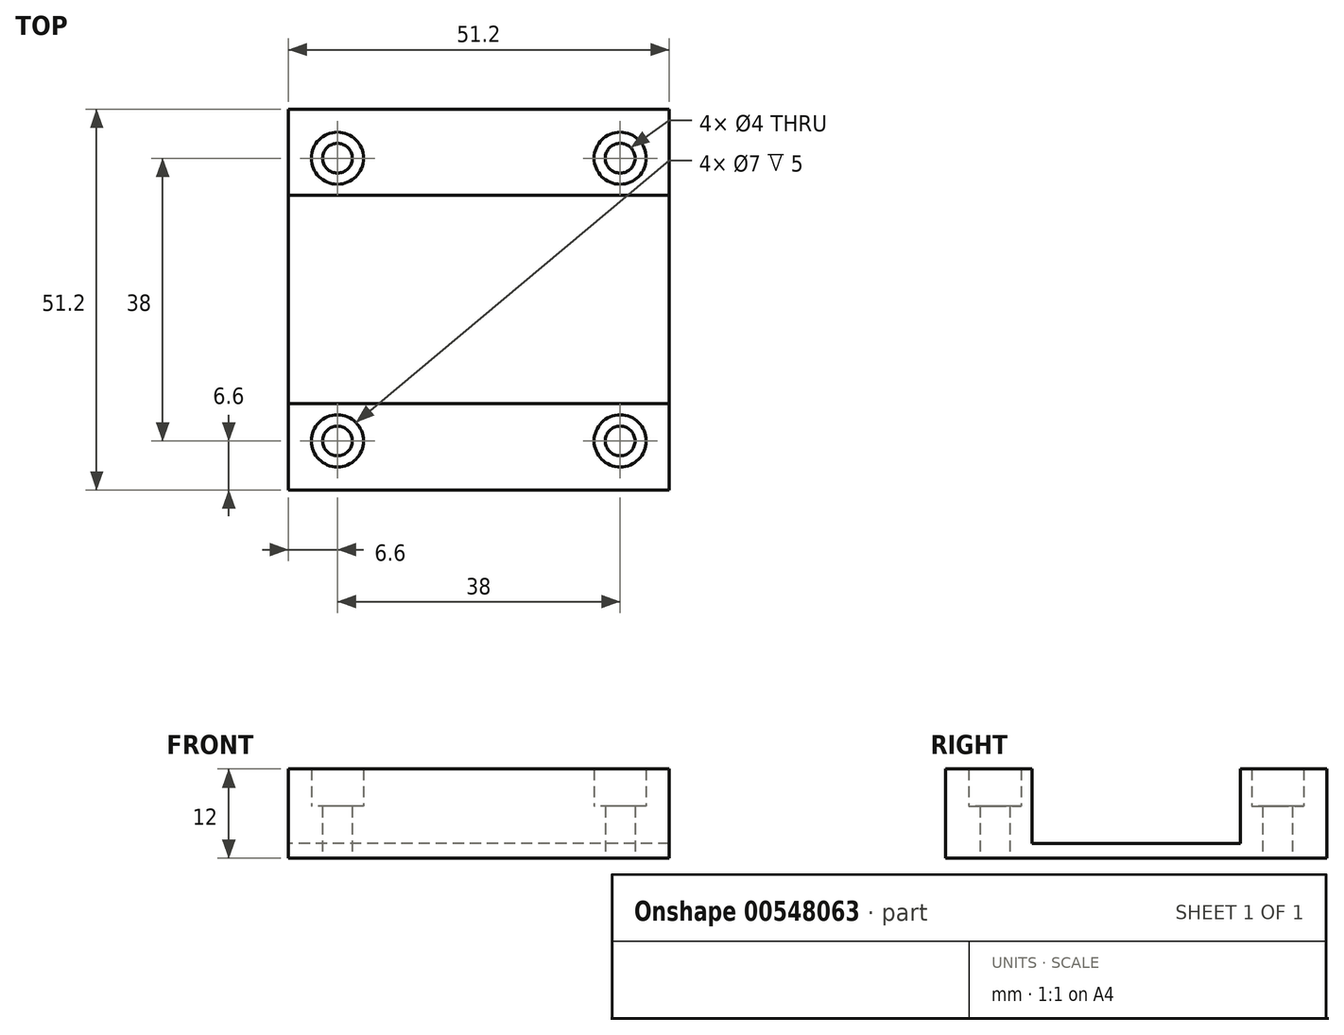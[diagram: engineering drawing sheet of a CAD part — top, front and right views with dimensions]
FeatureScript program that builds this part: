
annotation { "Feature Type Name" : "Feature", "Feature Type Description" : "" }
export const myFeature = defineFeature(function(context is Context, id is Id, definition is map)
    precondition{}
    {
        {
            var Q0;
            Q0=qCreatedBy(makeId("Top.planeOp"),FACE);
            var sketch = newSketch(context, id + "F0", { "sketchPlane" : qUnion([Q0])});
            skLineSegment(sketch, "E0.bottom", {"start": v(-25.6, 25.6) * mm, "end": v(25.6, 25.6) * mm});
            skLineSegment(sketch, "E0.top", {"start": v(-25.6, -25.6) * mm, "end": v(25.6, -25.6) * mm});
            skLineSegment(sketch, "E0.left", {"start": v(-25.6, 25.6) * mm, "end": v(-25.6, -25.6) * mm});
            skLineSegment(sketch, "E0.right", {"start": v(25.6, 25.6) * mm, "end": v(25.6, -25.6) * mm});
            skLineSegment(sketch, "E1", {"start": v(-25.6, 25.6) * mm, "end": v(25.6, -25.6) * mm, "construction": true});
            skLineSegment(sketch, "E2", {"start": v(-25.6, -25.6) * mm, "end": v(25.6, 25.6) * mm, "construction": true});
            skCircle(sketch, "E3", {"center": v(-19, 19) * mm, "radius": 2 * mm});
            skLineSegment(sketch, "E4", {"start": v(-19, 21) * mm, "end": v(-19, 25.6) * mm, "construction": true});
            skLineSegment(sketch, "E5", {"start": v(-21, 19) * mm, "end": v(-25.6, 19) * mm, "construction": true});
            skCircle(sketch, "E6.MirrorC", {"center": v(19, 19) * mm, "radius": 2 * mm});
            skLineSegment(sketch, "E7.MirrorCS", {"start": v(-21, -19) * mm, "end": v(-25.6, -19) * mm, "construction": true});
            skCircle(sketch, "E8.MirrorC", {"center": v(-19, -19) * mm, "radius": 2 * mm});
            skLineSegment(sketch, "E9.MirrorCS", {"start": v(-19, -21) * mm, "end": v(-19, -25.6) * mm, "construction": true});
            skCircle(sketch, "E10.MirrorC", {"center": v(19, -19) * mm, "radius": 2 * mm});
            skLineSegment(sketch, "E11", {"start": v(-25.6, 14) * mm, "end": v(25.6, 14) * mm});
            skLineSegment(sketch, "E12.MirrorCS", {"start": v(-25.6, -14) * mm, "end": v(25.6, -14) * mm});
            skSolve(sketch);
        }
        {
            var Q0;
            {var subQ1=sQuery(id+"F0.wireOp",EDGE,"E0.top");Q0=makeQuery(id+"F0.imprint","IMPRINT",FACE,{"disambiguationData":[TD([[makeQuery(id+"F0.imprint","IMPRINT",EDGE,{"derivedFrom":subQ1}),1.0]])]});}
            var Q1;
            {var subQ0=sQuery(id+"F0.wireOp",EDGE,"E11");Q1=makeQuery(id+"F0.imprint","IMPRINT",FACE,{"disambiguationData":[TD([[makeQuery(id+"F0.imprint","IMPRINT",EDGE,{"derivedFrom":subQ0}),-1.0]])]});}
            var Q2;
            {var subQ1=sQuery(id+"F0.wireOp",EDGE,"E0.bottom");Q2=makeQuery(id+"F0.imprint","IMPRINT",FACE,{"disambiguationData":[TD([[makeQuery(id+"F0.imprint","IMPRINT",EDGE,{"derivedFrom":subQ1}),-1.0]])]});}
            extrude(context, id + "F1", {"entities" : qUnion([Q0, Q1, Q2]), "depth" : 2 * mm, "offsetDistance" : 25 * mm});
        }
        {
            var Q0;
            Q0=makeQuery(id+"F1.opExtrude","CAP_FACE",FACE,{"disambiguationData":[OSD([sQuery(id+"F0.wireOp",EDGE,"E0.bottom"),sQuery(id+"F0.wireOp",EDGE,"E0.top"),sQuery(id+"F0.wireOp",EDGE,"E0.left"),sQuery(id+"F0.wireOp",EDGE,"E0.right"),sQuery(id+"F0.wireOp",EDGE,"E3"),sQuery(id+"F0.wireOp",EDGE,"E6.MirrorC"),sQuery(id+"F0.wireOp",EDGE,"E8.MirrorC"),sQuery(id+"F0.wireOp",EDGE,"E10.MirrorC")])],"isStart":false});
            var sketch = newSketch(context, id + "F2", { "sketchPlane" : qUnion([Q0])});
            skLineSegment(sketch, "E13.bottom", {"start": v(-25.6, 25.6) * mm, "end": v(25.6, 25.6) * mm});
            skLineSegment(sketch, "E13.top", {"start": v(-25.6, -25.6) * mm, "end": v(25.6, -25.6) * mm});
            skLineSegment(sketch, "E13.left", {"start": v(-25.6, 25.6) * mm, "end": v(-25.6, -25.6) * mm});
            skLineSegment(sketch, "E13.right", {"start": v(25.6, 25.6) * mm, "end": v(25.6, -25.6) * mm});
            skCircle(sketch, "E14", {"center": v(-19, 19) * mm, "radius": 2 * mm});
            skCircle(sketch, "E15.MirrorC", {"center": v(19, 19) * mm, "radius": 2 * mm});
            skCircle(sketch, "E16.MirrorC", {"center": v(19, -19) * mm, "radius": 2 * mm});
            skCircle(sketch, "E17.MirrorC", {"center": v(-19, -19) * mm, "radius": 2 * mm});
            skLineSegment(sketch, "E18", {"start": v(25.6, 14) * mm, "end": v(-25.6, 14) * mm});
            skLineSegment(sketch, "E19.MirrorCS", {"start": v(25.6, -14) * mm, "end": v(-25.6, -14) * mm});
            skSolve(sketch);
        }
        {
            var Q0;
            {var subQ1=sQuery(id+"F2.wireOp",EDGE,"E13.bottom");Q0=makeQuery(id+"F2.imprint","IMPRINT",FACE,{"disambiguationData":[TD([[makeQuery(id+"F2.imprint","IMPRINT",EDGE,{"derivedFrom":subQ1}),-1.0]])]});}
            var Q1;
            {var subQ1=sQuery(id+"F2.wireOp",EDGE,"E13.top");Q1=makeQuery(id+"F2.imprint","IMPRINT",FACE,{"disambiguationData":[TD([[makeQuery(id+"F2.imprint","IMPRINT",EDGE,{"derivedFrom":subQ1}),1.0]])]});}
            extrude(context, id + "F3", {"entities" : qUnion([Q0, Q1]), "operationType" : NewBodyOperationType.ADD, "depth" : 5 * mm, "offsetDistance" : 25 * mm});
        }
        {
            var Q0;
            Q0=makeQuery(id+"F3.opExtrude","CAP_FACE",FACE,{"disambiguationData":[OSD([sQuery(id+"F2.wireOp",EDGE,"E13.bottom"),sQuery(id+"F2.wireOp",EDGE,"E13.left"),sQuery(id+"F2.wireOp",EDGE,"E13.right"),sQuery(id+"F2.wireOp",EDGE,"E14"),sQuery(id+"F2.wireOp",EDGE,"E15.MirrorC"),sQuery(id+"F2.wireOp",EDGE,"E18")])],"isStart":false});
            var sketch = newSketch(context, id + "F4", { "sketchPlane" : qUnion([Q0])});
            skLineSegment(sketch, "E20.bottom", {"start": v(-25.6, 25.6) * mm, "end": v(25.6, 25.6) * mm});
            skLineSegment(sketch, "E20.top", {"start": v(-25.6, 14) * mm, "end": v(25.6, 14) * mm});
            skLineSegment(sketch, "E20.left", {"start": v(-25.6, 25.6) * mm, "end": v(-25.6, 14) * mm});
            skLineSegment(sketch, "E20.right", {"start": v(25.6, 25.6) * mm, "end": v(25.6, 14) * mm});
            skLineSegment(sketch, "E21.MirrorCS", {"start": v(25.6, -25.6) * mm, "end": v(25.6, -14) * mm});
            skLineSegment(sketch, "E22.MirrorCS", {"start": v(-25.6, -25.6) * mm, "end": v(-25.6, -14) * mm});
            skLineSegment(sketch, "E23.MirrorCS", {"start": v(-25.6, -14) * mm, "end": v(25.6, -14) * mm});
            skLineSegment(sketch, "E24.MirrorCS", {"start": v(-25.6, -25.6) * mm, "end": v(25.6, -25.6) * mm});
            skCircle(sketch, "E25", {"center": v(-19, 19) * mm, "radius": 3.5 * mm});
            skCircle(sketch, "E26.MirrorC", {"center": v(19, 19) * mm, "radius": 3.5 * mm});
            skCircle(sketch, "E27.MirrorC", {"center": v(19, -19) * mm, "radius": 3.5 * mm});
            skCircle(sketch, "E28.MirrorC", {"center": v(-19, -19) * mm, "radius": 3.5 * mm});
            skSolve(sketch);
        }
        {
            var Q0;
            Q0 = qSketchRegion(id + "F4", true);
            extrude(context, id + "F5", {"entities" : qUnion([Q0]), "operationType" : NewBodyOperationType.ADD, "depth" : 5 * mm, "offsetDistance" : 25 * mm});
        }
    });
